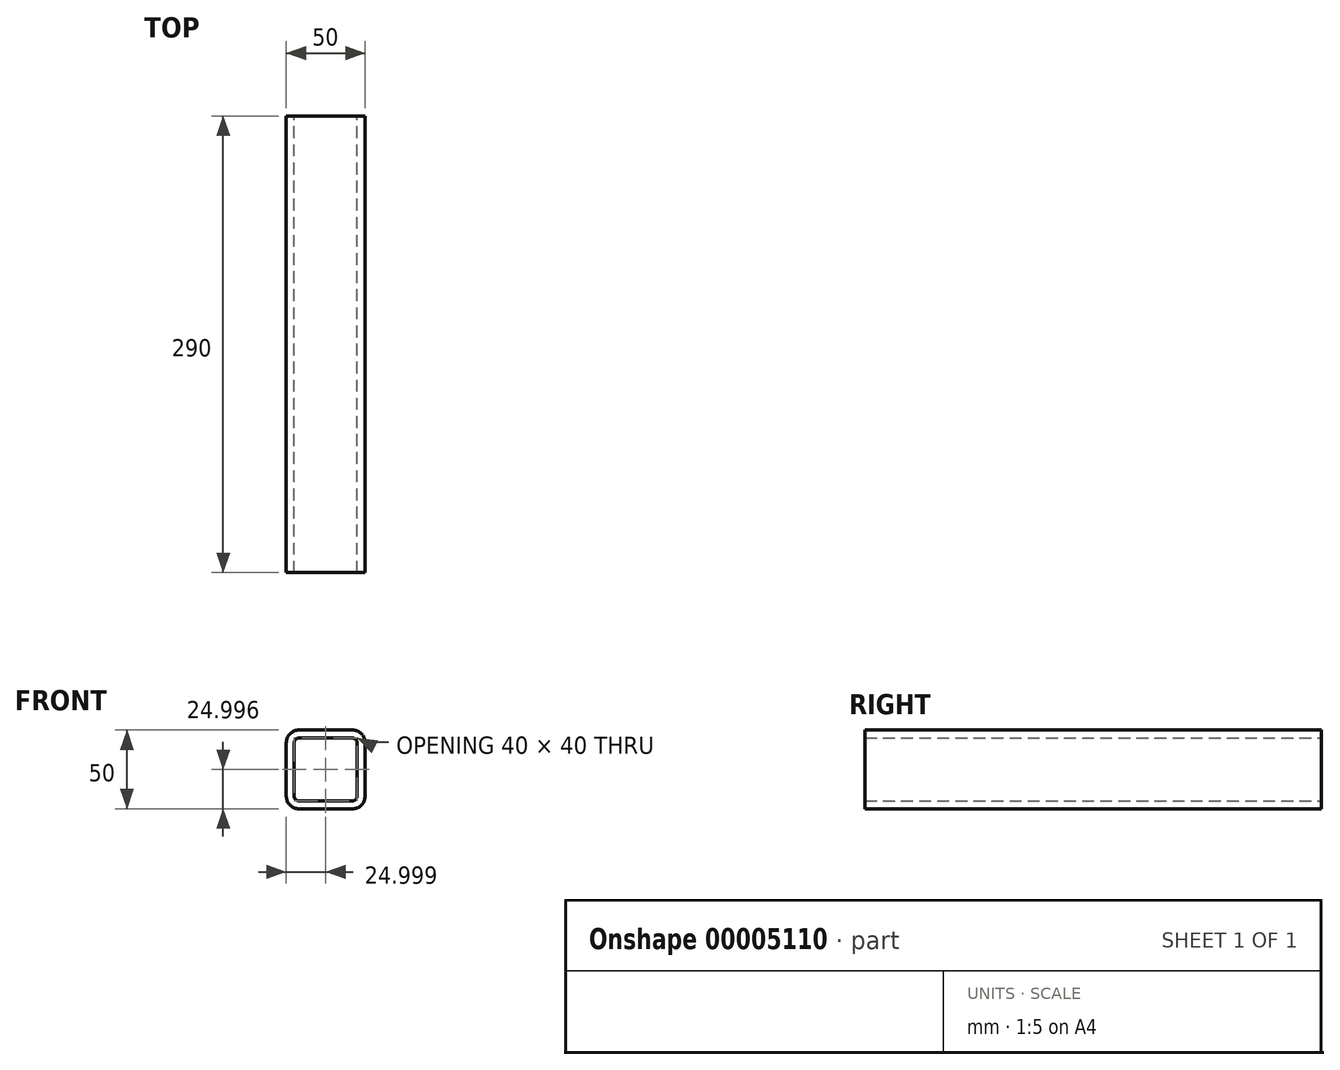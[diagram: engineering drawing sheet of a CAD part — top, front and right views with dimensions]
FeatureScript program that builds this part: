
annotation { "Feature Type Name" : "Feature", "Feature Type Description" : "" }
export const myFeature = defineFeature(function(context is Context, id is Id, definition is map)
    precondition{}
    {
        {
            var Q0;
            Q0=qCreatedBy(makeId("Front.planeOp"),FACE);
            var sketch = newSketch(context, id + "F0", { "sketchPlane" : qUnion([Q0])});
            skLineSegment(sketch, "E0.bottom", {"start": v(-56.43, 61.04) * mm, "end": v(-22.43, 61.04) * mm});
            skLineSegment(sketch, "E0.top", {"start": v(-56.43, 11.04) * mm, "end": v(-22.43, 11.04) * mm});
            skLineSegment(sketch, "E0.left", {"start": v(-64.43, 53.04) * mm, "end": v(-64.43, 19.04) * mm});
            skLineSegment(sketch, "E0.right", {"start": v(-14.43, 53.04) * mm, "end": v(-14.43, 19.04) * mm});
            skLineSegment(sketch, "E1.0", {"start": v(-59.43, 53.04) * mm, "end": v(-59.43, 19.04) * mm});
            skLineSegment(sketch, "E1.1", {"start": v(-56.43, 56.04) * mm, "end": v(-22.43, 56.04) * mm});
            skLineSegment(sketch, "E2.0", {"start": v(-19.43, 53.04) * mm, "end": v(-19.43, 19.04) * mm});
            skLineSegment(sketch, "E3.0", {"start": v(-56.43, 16.04) * mm, "end": v(-22.43, 16.04) * mm});
            skPoint(sketch, "E4.visualSharp", {"position": v(-14.43, 61.04) * mm});
            skArc(sketch, "E4.filletArc", {"start": v(-14.43, 53.04) * mm, "mid": v(-16.77, 58.7) * mm, "end": v(-22.43, 61.04) * mm});
            skPoint(sketch, "E5.visualSharp", {"position": v(-64.43, 61.04) * mm});
            skArc(sketch, "E5.filletArc", {"start": v(-56.43, 61.04) * mm, "mid": v(-62.09, 58.7) * mm, "end": v(-64.43, 53.04) * mm});
            skPoint(sketch, "E6.visualSharp", {"position": v(-64.43, 11.04) * mm});
            skArc(sketch, "E6.filletArc", {"start": v(-64.43, 19.04) * mm, "mid": v(-62.09, 13.38) * mm, "end": v(-56.43, 11.04) * mm});
            skPoint(sketch, "E7.visualSharp", {"position": v(-14.43, 11.04) * mm});
            skArc(sketch, "E7.filletArc", {"start": v(-22.43, 11.04) * mm, "mid": v(-16.77, 13.38) * mm, "end": v(-14.43, 19.04) * mm});
            skPoint(sketch, "E8.visualSharp", {"position": v(-59.43, 56.04) * mm});
            skArc(sketch, "E8.filletArc", {"start": v(-56.43, 56.04) * mm, "mid": v(-58.55, 55.16) * mm, "end": v(-59.43, 53.04) * mm});
            skPoint(sketch, "E9.visualSharp", {"position": v(-59.43, 16.04) * mm});
            skArc(sketch, "E9.filletArc", {"start": v(-59.43, 19.04) * mm, "mid": v(-58.55, 16.91) * mm, "end": v(-56.43, 16.04) * mm});
            skPoint(sketch, "E10.visualSharp", {"position": v(-19.43, 16.04) * mm});
            skArc(sketch, "E10.filletArc", {"start": v(-22.43, 16.04) * mm, "mid": v(-20.3, 16.91) * mm, "end": v(-19.43, 19.04) * mm});
            skArc(sketch, "E11.filletArc", {"start": v(-19.43, 53.04) * mm, "mid": v(-20.3, 55.16) * mm, "end": v(-22.43, 56.04) * mm});
            skSolve(sketch);
        }
        {
            var Q0;
            Q0=makeQuery(id+"F0.imprint","IMPRINT",FACE,{"disambiguationData":[TD([[makeQuery(id+"F0.imprint","IMPRINT",EDGE,{"derivedFrom":sQuery(id+"F0.wireOp",EDGE,"E0.bottom")}),-1.0]])]});
            extrude(context, id + "F1", {"entities" : qUnion([Q0]), "depth" : 290 * mm});
        }
    });
